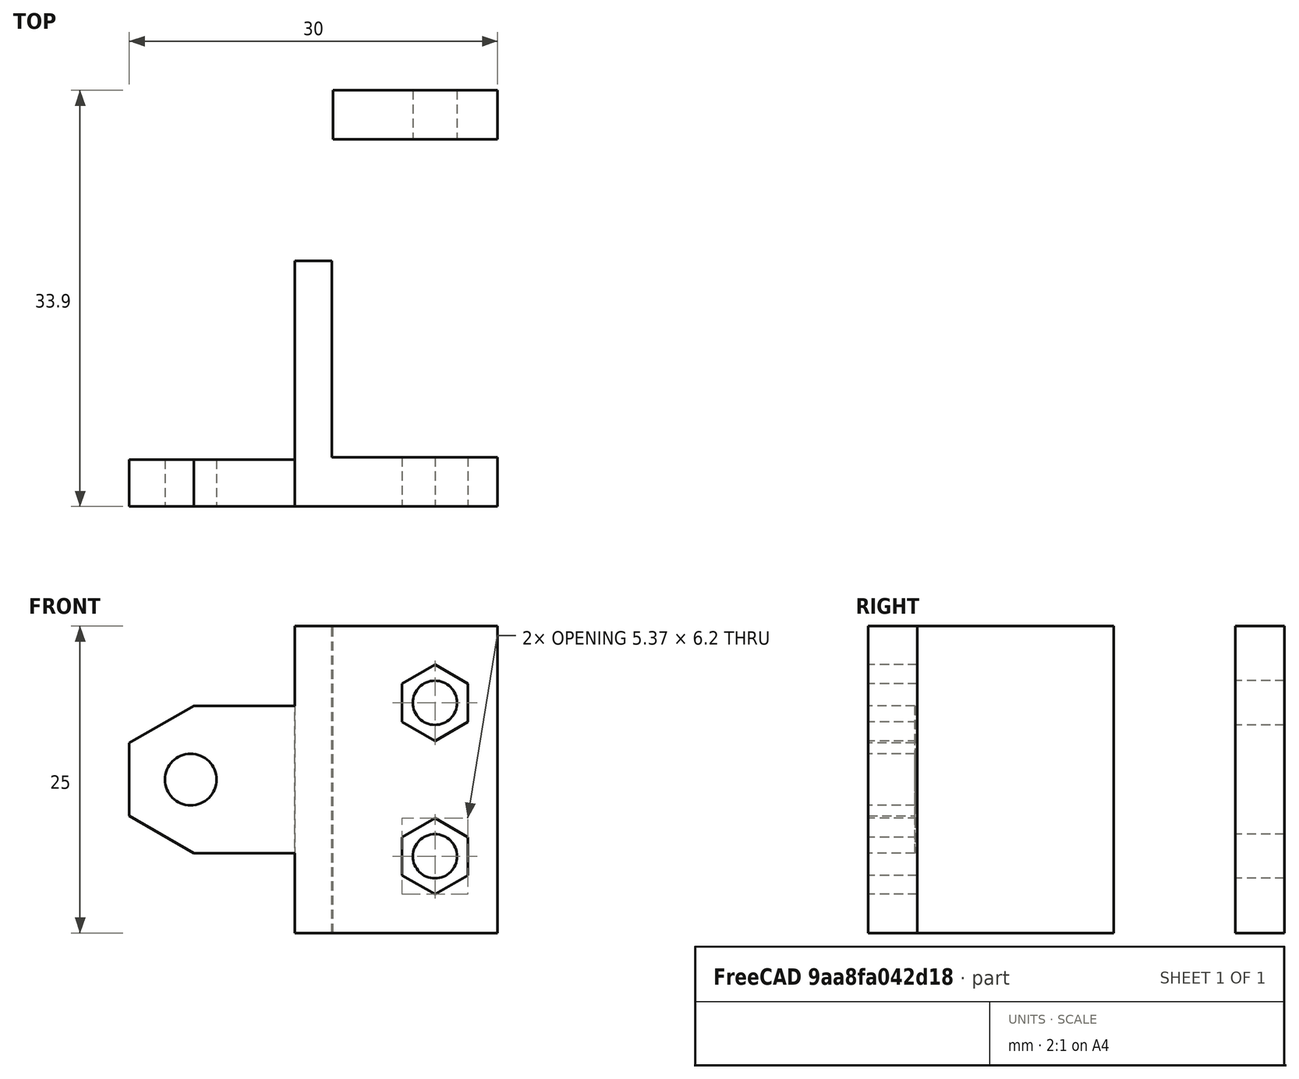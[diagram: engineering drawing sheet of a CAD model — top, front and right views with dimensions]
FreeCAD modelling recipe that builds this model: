
FCSTD DOCUMENT  (FreeCAD 0.19R23634 (Git))
Label: Stage-Manipulator
License: All rights reserved
LicenseURL: http://en.wikipedia.org/wiki/All_rights_reserved
objects: Part::Box×4, Part::Prism×4, Part::Cylinder×3, Part::MultiFuse×2, Part::Cut×1, PartDesign::FeatureBase×1, PartDesign::CoordinateSystem×1, PartDesign::Body×1, App::Part×1
note: 17 computed .brp shape members not serialized (recipe doc carries the construction recipe); baked Part::Feature solids carry a one-line shape summary decoded from their .brp

FEATURE [Part::Box] cube027
  AttacherType = Attacher::AttachEngine3D
  Height = 25
  Length = 13.4
  Placement = pos=(56.6,85.5,53.5) rot=(0,0,1;0rad)
  Width = 4
FEATURE [Part::Prism] prism018
  AttacherType = Attacher::AttachEngine3D
  Circumradius = 5.25
  FirstAngle = 0
  Height = 13
  Placement = pos=(40,64,72) rot=(1,0,0;1.5708rad)
  Polygon = 3
  SecondAngle = 0
FEATURE [Part::Box] cube024
  AttacherType = Attacher::AttachEngine3D
  Height = 12
  Length = 15
  Placement = pos=(40,55.6,60) rot=(0,0,1;0rad)
  Width = 3.8
FEATURE [Part::Prism] prism020
  AttacherType = Attacher::AttachEngine3D
  Circumradius = 3.1
  FirstAngle = 0
  Height = 6
  Placement = pos=(64.9,60.5,72.25) rot=(0.935113,0.250563,-0.250563;1.63783rad)
  Polygon = 6
  SecondAngle = 0
FEATURE [Part::Box] cube025
  AttacherType = Attacher::AttachEngine3D
  Height = 25
  Length = 3
  Placement = pos=(53.5,55.6,53.5) rot=(0,0,1;0rad)
  Width = 20
FEATURE [Part::Prism] prism021
  AttacherType = Attacher::AttachEngine3D
  Circumradius = 3.1
  FirstAngle = 0
  Height = 6
  Placement = pos=(64.9,60.5,59.75) rot=(0.935113,0.250563,-0.250563;1.63783rad)
  Polygon = 6
  SecondAngle = 0
FEATURE [Part::Cylinder] cylinder016
  Angle = 360
  AttacherType = Attacher::AttachEngine3D
  Height = 6
  Placement = pos=(64.9,90.5,72.25) rot=(1,0,0;1.5708rad)
  Radius = 1.8
FEATURE [Part::Box] cube026
  AttacherType = Attacher::AttachEngine3D
  Height = 25
  Length = 15
  Placement = pos=(55,55.6,53.5) rot=(0,0,1;0rad)
  Width = 4
FEATURE [Part::Cylinder] cylinder017
  Angle = 360
  AttacherType = Attacher::AttachEngine3D
  Height = 6
  Placement = pos=(64.9,90.5,59.75) rot=(1,0,0;1.5708rad)
  Radius = 1.8
FEATURE [Part::Cylinder] cylinder015
  Angle = 360
  AttacherType = Attacher::AttachEngine3D
  Height = 13
  Placement = pos=(45,64,66) rot=(1,0,0;1.5708rad)
  Radius = 2.1
FEATURE [Part::Prism] prism019
  AttacherType = Attacher::AttachEngine3D
  Circumradius = 5.25
  FirstAngle = 0
  Height = 13
  Placement = pos=(40,64,60) rot=(1,0,0;1.5708rad)
  Polygon = 3
  SecondAngle = 0
FEATURE [Part::MultiFuse] Group011
  Shapes = -> [cylinder015,prism018,prism019,prism020,cylinder016,prism021,cylinder017]
FEATURE [Part::MultiFuse] Group010
  Shapes = -> [cube024,cube025,cube026,cube027]
FEATURE [Part::Cut] difference006
  Base = -> Group010
  Tool = -> Group011
FEATURE [PartDesign::FeatureBase] BaseFeature006
  BaseFeature = -> difference006
FEATURE [PartDesign::CoordinateSystem] LCS_0
  AttacherType = Attacher::AttachEngine3D
  MapMode = 45
  Placement = pos=(55.75,57.6,53.5) rot=(0,0,1;0rad)
  Support = -> [BaseFeature006]
FEATURE [PartDesign::Body] Body006  label="Manipulator001"
  BaseFeature = -> difference006
  Group = -> [BaseFeature006]
  Origin = -> Origin006
  Tip = -> BaseFeature006
FEATURE [App::Part] Manipulator
  Group = -> [LCS_0,cube027,cube024,prism018,prism020,Group011,cube025,prism021,cylinder016,cube026,cylinder017,difference006,cylinder015,prism019,Group010,Body006]
  Origin = -> Origin
